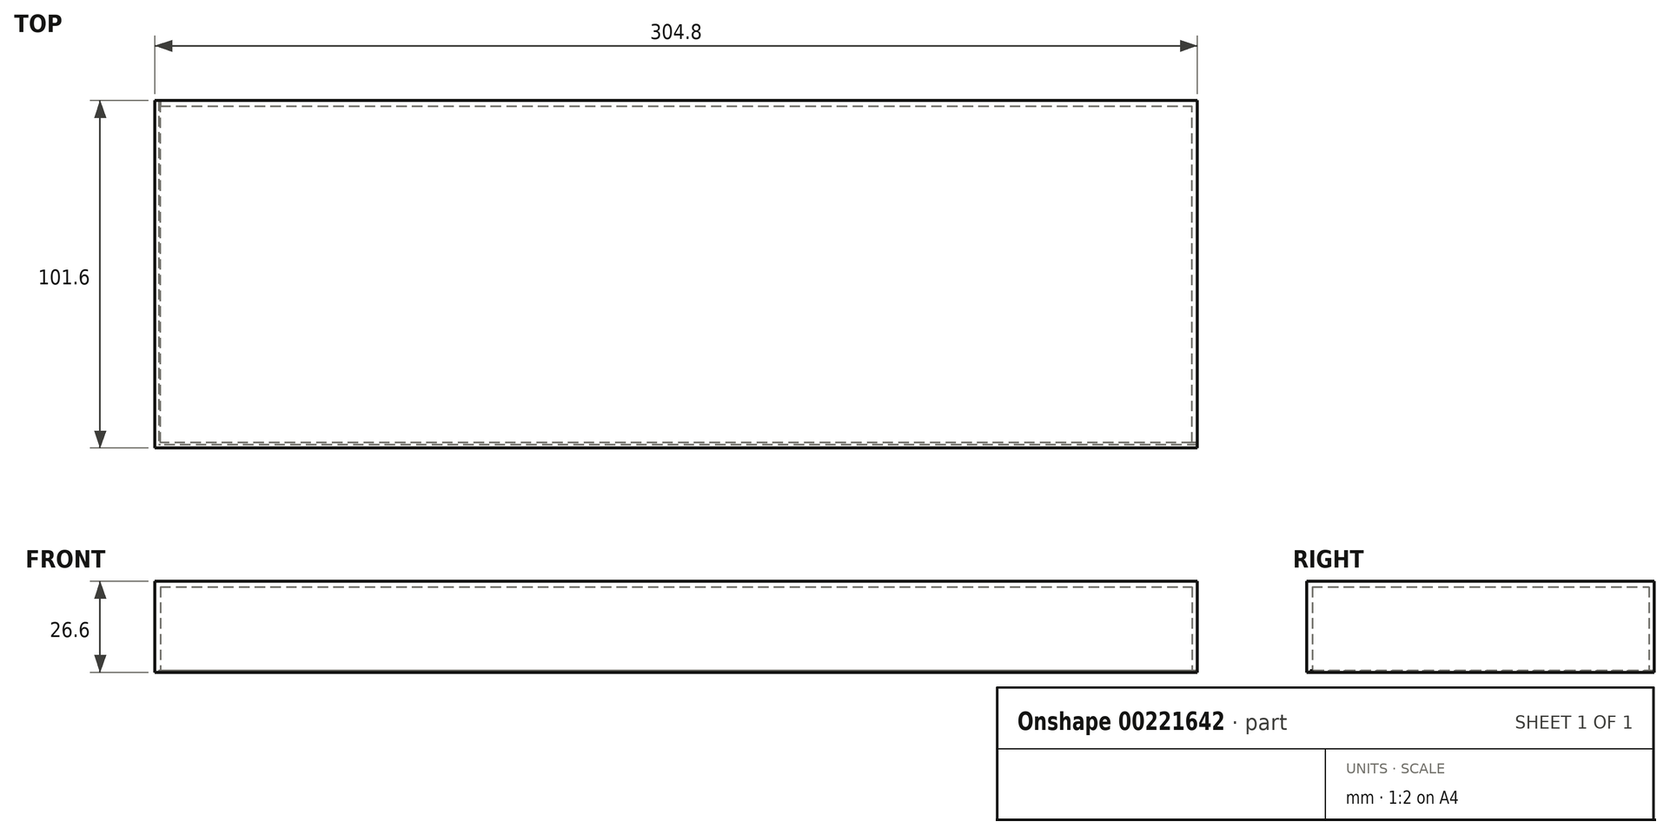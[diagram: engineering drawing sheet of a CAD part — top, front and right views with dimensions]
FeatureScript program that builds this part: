
annotation { "Feature Type Name" : "Feature", "Feature Type Description" : "" }
export const myFeature = defineFeature(function(context is Context, id is Id, definition is map)
    precondition{}
    {
        {
            var Q0;
            Q0=qCreatedBy(makeId("Top.planeOp"),FACE);
            var sketch = newSketch(context, id + "F0", { "sketchPlane" : qUnion([Q0])});
            skLineSegment(sketch, "E0.bottom", {"start": v(-148.4, -148.19) * mm, "end": v(156.4, -148.19) * mm});
            skLineSegment(sketch, "E0.top", {"start": v(-148.4, -46.59) * mm, "end": v(156.4, -46.59) * mm});
            skLineSegment(sketch, "E0.left", {"start": v(-148.4, -148.19) * mm, "end": v(-148.4, -46.59) * mm});
            skLineSegment(sketch, "E0.right", {"start": v(156.4, -148.19) * mm, "end": v(156.4, -46.59) * mm});
            skLineSegment(sketch, "E1.0", {"start": v(154.8, -146.59) * mm, "end": v(154.8, -48.19) * mm});
            skLineSegment(sketch, "E1.1", {"start": v(-146.8, -146.59) * mm, "end": v(154.8, -146.59) * mm});
            skLineSegment(sketch, "E1.2", {"start": v(-146.8, -146.59) * mm, "end": v(-146.8, -48.19) * mm});
            skLineSegment(sketch, "E1.3", {"start": v(-146.8, -48.19) * mm, "end": v(154.8, -48.19) * mm});
            skSolve(sketch);
        }
        {
            var Q0;
            Q0=makeQuery(id+"F0.imprint","IMPRINT",FACE,{"disambiguationData":[TD([[makeQuery(id+"F0.imprint","IMPRINT",EDGE,{"derivedFrom":sQuery(id+"F0.wireOp",EDGE,"E0.bottom")}),1.0]])]});
            extrude(context, id + "F1", {"entities" : qUnion([Q0]), "depth" : 25 * mm});
        }
        {
            var Q0;
            Q0=makeQuery(id+"F1.opExtrude","CAP_FACE",FACE,{"disambiguationData":[OSD([sQuery(id+"F0.wireOp",EDGE,"E0.bottom"),sQuery(id+"F0.wireOp",EDGE,"E0.top"),sQuery(id+"F0.wireOp",EDGE,"E0.left"),sQuery(id+"F0.wireOp",EDGE,"E0.right"),sQuery(id+"F0.wireOp",EDGE,"E1.0"),sQuery(id+"F0.wireOp",EDGE,"E1.1"),sQuery(id+"F0.wireOp",EDGE,"E1.2"),sQuery(id+"F0.wireOp",EDGE,"E1.3")])],"isStart":false});
            var sketch = newSketch(context, id + "F2", { "sketchPlane" : qUnion([Q0])});
            skLineSegment(sketch, "E2.bottom", {"start": v(156.4, -46.59) * mm, "end": v(-148.4, -46.59) * mm});
            skLineSegment(sketch, "E2.top", {"start": v(156.4, -148.19) * mm, "end": v(-148.4, -148.19) * mm});
            skLineSegment(sketch, "E2.left", {"start": v(156.4, -46.59) * mm, "end": v(156.4, -148.19) * mm});
            skLineSegment(sketch, "E2.right", {"start": v(-148.4, -46.59) * mm, "end": v(-148.4, -148.19) * mm});
            skSolve(sketch);
        }
        {
            var Q0;
            Q0 = qSketchRegion(id + "F2", true);
            extrude(context, id + "F3", {"entities" : qUnion([Q0]), "operationType" : NewBodyOperationType.ADD, "depth" : 1.6 * mm});
        }
        {
            var Q0;
            Q0=makeQuery(id+"F1.opExtrude","SWEPT_FACE",FACE,{"disambiguationData":[OSD([sQuery(id+"F0.wireOp",EDGE,"E1.2")])]});
            var sketch = newSketch(context, id + "F4", { "sketchPlane" : qUnion([Q0])});
            skLineSegment(sketch, "E3.bottom", {"start": v(-146.59, 0) * mm, "end": v(-147.23, 0) * mm});
            skLineSegment(sketch, "E3.top", {"start": v(-146.59, 0.5) * mm, "end": v(-147.23, 0.5) * mm});
            skLineSegment(sketch, "E3.left", {"start": v(-146.59, 0) * mm, "end": v(-146.59, 0.5) * mm});
            skLineSegment(sketch, "E3.right", {"start": v(-147.23, 0) * mm, "end": v(-147.23, 0.5) * mm});
            skSolve(sketch);
        }
        {
            var Q0;
            Q0 = qSketchRegion(id + "F4", true);
            extrude(context, id + "F5", {"entities" : qUnion([Q0]), "operationType" : NewBodyOperationType.REMOVE, "endBound" : BoundingType.UP_TO_NEXT, "depth" : 25 * mm});
        }
        {
            var Q0;
            Q0=makeQuery(id+"F5.boolean.opBoolean","COPY",FACE,{"derivedFrom":makeQuery(id+"F5.opExtrude","SWEPT_FACE",FACE,{"disambiguationData":[OSD([sQuery(id+"F4.wireOp",EDGE,"E3.right")])]})});
            var sketch = newSketch(context, id + "F6", { "sketchPlane" : qUnion([Q0])});
            skLineSegment(sketch, "E4.bottom", {"start": v(146.8, 0) * mm, "end": v(147.32, 0) * mm});
            skLineSegment(sketch, "E4.top", {"start": v(146.8, 0.5) * mm, "end": v(147.32, 0.5) * mm});
            skLineSegment(sketch, "E4.left", {"start": v(146.8, 0) * mm, "end": v(146.8, 0.5) * mm});
            skLineSegment(sketch, "E4.right", {"start": v(147.32, 0) * mm, "end": v(147.32, 0.5) * mm});
            skSolve(sketch);
        }
        {
            var Q0;
            Q0 = qSketchRegion(id + "F6", true);
            extrude(context, id + "F7", {"entities" : qUnion([Q0]), "operationType" : NewBodyOperationType.REMOVE, "endBound" : BoundingType.UP_TO_NEXT, "depth" : 25 * mm});
        }
    });
